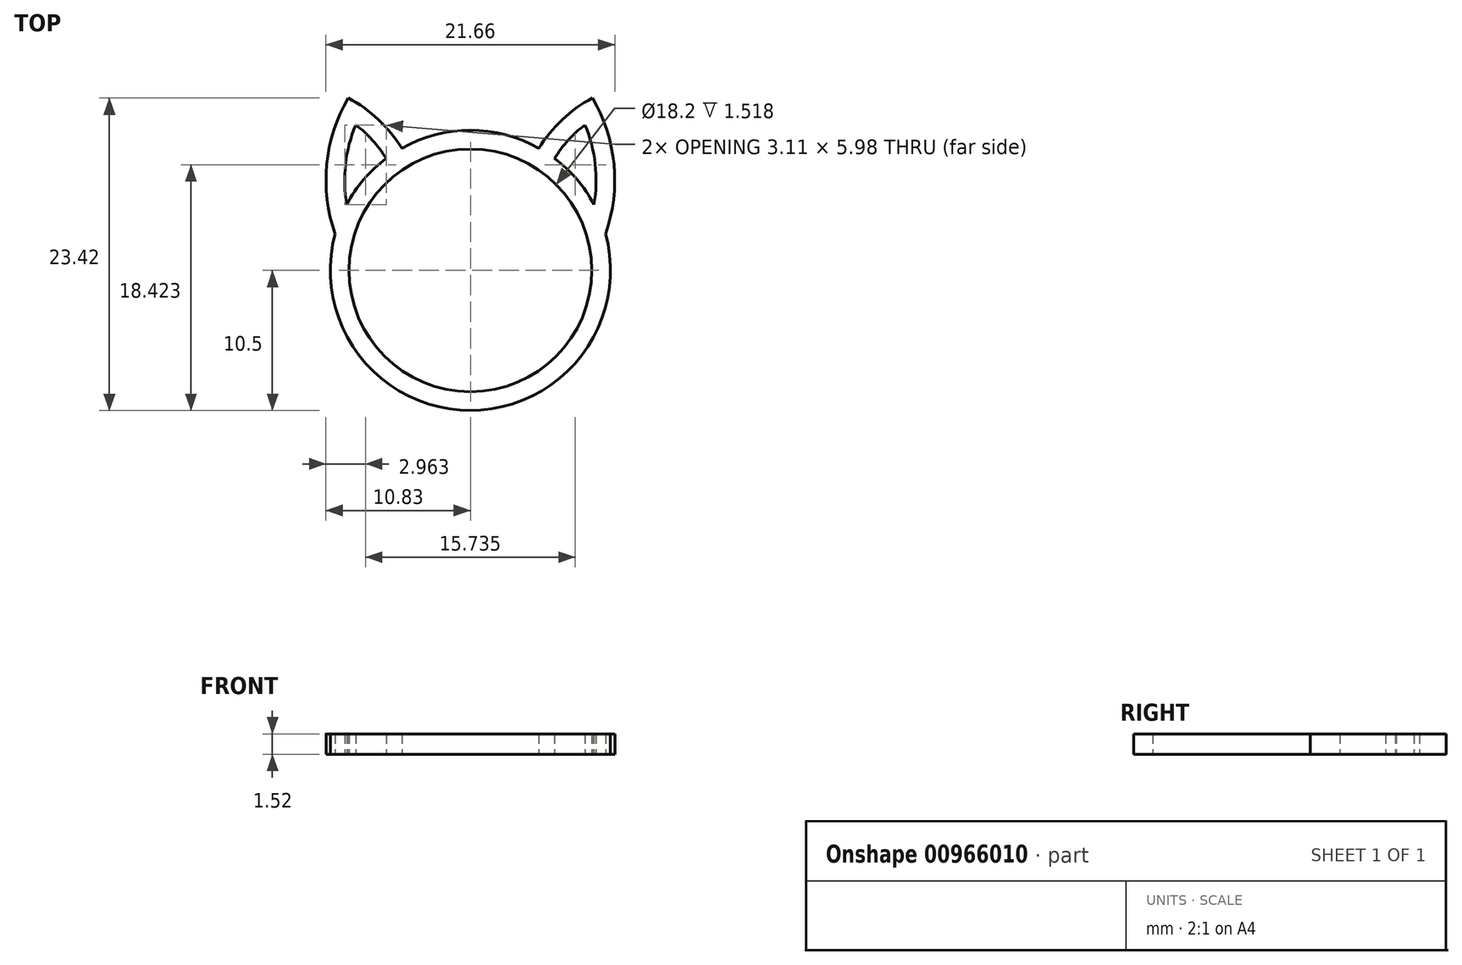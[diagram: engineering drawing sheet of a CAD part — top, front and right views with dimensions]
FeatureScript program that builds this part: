
annotation { "Feature Type Name" : "Feature", "Feature Type Description" : "" }
export const myFeature = defineFeature(function(context is Context, id is Id, definition is map)
    precondition{}
    {
        {
            var Q0;
            Q0=qCreatedBy(makeId("Top.planeOp"),FACE);
            var sketch = newSketch(context, id + "F0", { "sketchPlane" : qUnion([Q0])});
            skCircle(sketch, "E0", {"center": v(0, 0) * mm, "radius": 8.45 * mm});
            skCircle(sketch, "E1", {"center": v(0, 0) * mm, "radius": 9.75 * mm});
            skArc(sketch, "E2", {"start": v(9.41, 2.54) * mm, "mid": v(10, 7.37) * mm, "end": v(8.5, 12) * mm});
            skArc(sketch, "E3", {"start": v(8.5, 12) * mm, "mid": v(6.4, 10.5) * mm, "end": v(4.77, 8.5) * mm});
            skArc(sketch, "E4.0", {"start": v(7.98, 10.13) * mm, "mid": v(6.8, 9.06) * mm, "end": v(5.86, 7.8) * mm});
            skArc(sketch, "E4.1", {"start": v(8.6, 4.58) * mm, "mid": v(8.69, 7.4) * mm, "end": v(7.98, 10.13) * mm});
            skArc(sketch, "E5.MirrorCS", {"start": v(-8.5, 12) * mm, "mid": v(-6.4, 10.5) * mm, "end": v(-4.77, 8.5) * mm});
            skArc(sketch, "E6.MirrorCS", {"start": v(-9.41, 2.54) * mm, "mid": v(-10, 7.37) * mm, "end": v(-8.5, 12) * mm});
            skArc(sketch, "E7.MirrorCS", {"start": v(-7.98, 10.13) * mm, "mid": v(-6.8, 9.06) * mm, "end": v(-5.86, 7.8) * mm});
            skArc(sketch, "E8.MirrorCS", {"start": v(-8.6, 4.58) * mm, "mid": v(-8.69, 7.4) * mm, "end": v(-7.98, 10.13) * mm});
            skSolve(sketch);
        }
        {
            var Q0;
            Q0=qSketchRegion(id+"F0",true);
            extrude(context, id + "F1", {"entities" : qUnion([Q0]), "depth" : 1.4 * mm, "offsetDistance" : 25.4 * mm});
        }
        {
            var Q0;
            Q0=makeQuery(id+"F1.opExtrude","SWEPT_BODY",BODY,{"disambiguationData":[OSD([sQuery(id+"F0.wireOp",EDGE,"E0"),sQuery(id+"F0.wireOp",EDGE,"E1"),sQuery(id+"F0.wireOp",EDGE,"E2"),sQuery(id+"F0.wireOp",EDGE,"E3"),sQuery(id+"F0.wireOp",EDGE,"E4.0"),sQuery(id+"F0.wireOp",EDGE,"E4.1"),sQuery(id+"F0.wireOp",EDGE,"E5.MirrorCS"),sQuery(id+"F0.wireOp",EDGE,"E6.MirrorCS"),sQuery(id+"F0.wireOp",EDGE,"E7.MirrorCS"),sQuery(id+"F0.wireOp",EDGE,"E8.MirrorCS")])]});
            var Q1;
            Q1=qCreatedBy(makeId("Origin.pointOp"),VERTEX);
            transform(context, id + "F2", {"entities" : qUnion([Q0]), "transformType" : TransformType.SCALE_UNIFORMLY, "scale" : 1.08, "scalePoint" : qUnion([Q1]), "makeCopy" : false});
        }
    });
